# Revit family: ZPT24
name_source: partatom
category: Lighting Fixtures
revit_build: Autodesk Revit Architecture 2012 (Build: 20110309_2315(x64)
units: mm (PartAtom-declared; Revit-internal decimal feet)

## types (18) — shared parameters
Backbox = White
Color Filter = 16777215
Default Elevation = 48.000"
Description = Zero Plenum® Troffer High Efficiency Architectural Luminaire
Dimming Lamp Color Temperature Shift = <None>
Emit Shape Visible in Rendering = No
Emit from Rectangle Length = 48.000"
Emit from Rectangle Width = 24.000"
Glass = Glass
Lamp = F28T8
Manufacturer = Columbia Lighting
Manufacturer Fax = 866-898-1065
Model = ZPT22
Product Documentation Link = http://www.columbialighting.com
Product Page URL = http://www.columbialighting.com
Tilt Angle = -90.00°
URL = http://www.columbialighting.com
Wattage Comments = 60 W

## per-type parameters (varying)
| type | Photometric Web File |
| ZPT24-228G-FCBO | 14318 |
| ZPT24-228G-FCBR | 14278 |
| ZPT24-228G-FCBS | 14277 |
| ZPT24-228G-LSRO | 13992 |
| ZPT24-228G-LSRR | 14584 |
| ZPT24-228G-LSRR-EP | 13996 |
| ZPT24-228G-LSRS | 13975 |
| ZPT24-228G-PRFR | 14276 |
| ZPT24-228G-PRFS | 13995 |
| ZPT24-254G-FCBO | 14233 |
| ZPT24-254G-FCBR | 14273 |
| ZPT24-254G-FCBS | 14275 |
| ZPT24-254G-LSRO | 14280 |
| ZPT24-254G-LSRR | 14282 |
| ZPT24-254G-LSRS | 14281 |
| ZPT24-254G-PRFR | 14274 |
| ZPT24-254G-PRFS | 14279 |
| type_17 |  |

## geometry (parser evidence)
native form markers: Sweep x1
no freeform markers — native parametric forms only
